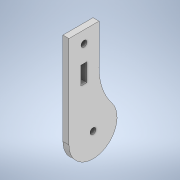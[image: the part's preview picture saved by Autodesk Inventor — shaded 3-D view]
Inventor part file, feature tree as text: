
AUTODESK INVENTOR PART (.ipt)
format: ipt  version: 2022 (Build 260153000, 153)  size: 125,952 bytes
history: native  units: mm
features: extrude x1, sketch x1
ambient origin geometry x8: Origin, YZ Plane, XZ Plane, XY Plane, X Axis, Y Axis, Z Axis, Center Point
bodies: Solid1 (feature_tree)
feature tree (2):
  extrude  "Extrusion1"  Depth=9.0mm
  sketch  "Sketch1"  dims[d9=58.0mm d14=3.0mm d15=0.0mm d18=9.0mm d19=3.0mm d20=6.0mm d21=7.5mm d22=3.0mm d23=15.0mm d24=12.0mm d25=8.5mm]
